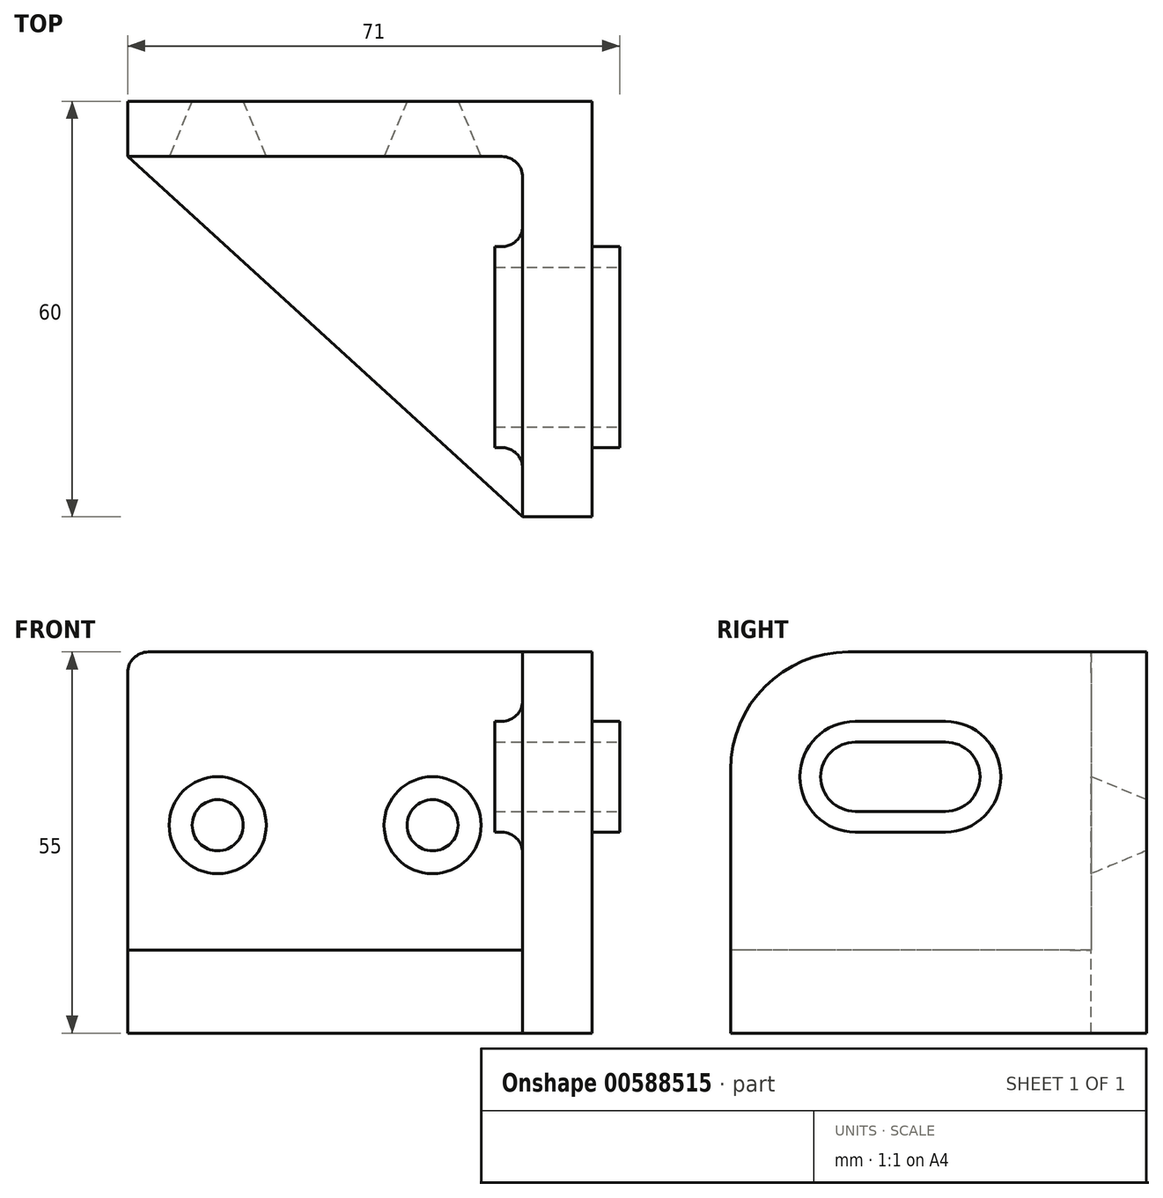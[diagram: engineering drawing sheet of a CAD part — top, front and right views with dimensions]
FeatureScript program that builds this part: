
annotation { "Feature Type Name" : "Feature", "Feature Type Description" : "" }
export const myFeature = defineFeature(function(context is Context, id is Id, definition is map)
    precondition{}
    {
        {
            var Q0;
            Q0=qCreatedBy(makeId("Top.planeOp"),FACE);
            var sketch = newSketch(context, id + "F0", { "sketchPlane" : qUnion([Q0])});
            skLineSegment(sketch, "E0.bottom", {"start": v(0, 0) * mm, "end": v(67, 0) * mm});
            skLineSegment(sketch, "E0.top", {"start": v(57, -60) * mm, "end": v(67, -60) * mm});
            skLineSegment(sketch, "E0.left", {"start": v(0, 0) * mm, "end": v(0, -8) * mm});
            skLineSegment(sketch, "E0.right", {"start": v(67, 0) * mm, "end": v(67, -60) * mm});
            skLineSegment(sketch, "E1", {"start": v(0, -8) * mm, "end": v(57, -60) * mm});
            skLineSegment(sketch, "E2", {"start": v(0, -8) * mm, "end": v(57, -8) * mm});
            skLineSegment(sketch, "E3", {"start": v(57, -8) * mm, "end": v(57, -60) * mm});
            skLineSegment(sketch, "E4.bottom", {"start": v(67, 0) * mm, "end": v(0, 0) * mm});
            skLineSegment(sketch, "E4.top", {"start": v(67, 5) * mm, "end": v(0, 5) * mm});
            skLineSegment(sketch, "E4.left", {"start": v(67, 0) * mm, "end": v(67, 5) * mm});
            skLineSegment(sketch, "E4.right", {"start": v(0, 0) * mm, "end": v(0, 5) * mm});
            skSolve(sketch);
        }
        {
            var Q0;
            {var subQ1=sQuery(id+"F0.wireOp",EDGE,"E1");Q0=makeQuery(id+"F0.imprint","IMPRINT",FACE,{"disambiguationData":[TD([[makeQuery(id+"F0.imprint","IMPRINT",EDGE,{"derivedFrom":subQ1}),1.0]])]});}
            var Q1;
            Q1=makeQuery(id+"F0.imprint","IMPRINT",FACE,{"disambiguationData":[TD([[makeQuery(id+"F0.imprint","IMPRINT",EDGE,{"derivedFrom":sQuery(id+"F0.wireOp",EDGE,"E0.left")}),1.0]])]});
            var Q2;
            Q2=makeQuery(id+"F0.imprint","IMPRINT",FACE,{"disambiguationData":[TD([[makeQuery(id+"F0.imprint","IMPRINT",EDGE,{"derivedFrom":sQuery(id+"F0.wireOp",EDGE,"E4.bottom")}),-1.0]])]});
            var Q3;
            {var subQ0=sQuery(id+"F0.wireOp",EDGE,"E0.top");Q3=makeQuery(id+"F0.imprint","IMPRINT",FACE,{"disambiguationData":[TD([[makeQuery(id+"F0.imprint","IMPRINT",EDGE,{"derivedFrom":subQ0}),1.0]])]});}
            var Q4;
            {var subQ0=sQuery(id+"F0.wireOp",EDGE,"VNKDlEv6-xTZ3-Mihn-J32e-wtWmNRO4bZqF.bottom");var subQ1=sQuery(id+"F0.wireOp",EDGE,"E0.right");var subQ2=makeQuery(id+"F0.imprint","INTERSECT",VERTEX,{"derivedFrom":[subQ1,subQ0]});Q4=makeQuery(id+"F0.imprint","IMPRINT",FACE,{"disambiguationData":[TD([[makeQuery(id+"F0.imprint","IMPRINT",EDGE,{"disambiguationData":[TD([[subQ2,-1.0]])],"derivedFrom":subQ1}),-1.0]])]});}
            var Q5;
            {var subQ5=sQuery(id+"F0.wireOp",EDGE,"VNKDlEv6-xTZ3-Mihn-J32e-wtWmNRO4bZqF.right");Q5=makeQuery(id+"F0.imprint","IMPRINT",FACE,{"disambiguationData":[TD([[makeQuery(id+"F0.imprint","IMPRINT",EDGE,{"derivedFrom":subQ5}),1.0]])]});}
            extrude(context, id + "F1", {"entities" : qUnion([Q0, Q1, Q2, Q3, Q4, Q5]), "oppositeDirection" : true, "depth" : 12 * mm, "offsetDistance" : 25 * mm});
        }
        {
            var Q0;
            Q0=makeQuery(id+"F0.imprint","IMPRINT",FACE,{"disambiguationData":[TD([[makeQuery(id+"F0.imprint","IMPRINT",EDGE,{"derivedFrom":sQuery(id+"F0.wireOp",EDGE,"E0.left")}),1.0]])]});
            var Q1;
            Q1=makeQuery(id+"F0.imprint","IMPRINT",FACE,{"disambiguationData":[TD([[makeQuery(id+"F0.imprint","IMPRINT",EDGE,{"derivedFrom":sQuery(id+"F0.wireOp",EDGE,"E4.bottom")}),-1.0]])]});
            var Q2;
            {var subQ0=sQuery(id+"F0.wireOp",EDGE,"VNKDlEv6-xTZ3-Mihn-J32e-wtWmNRO4bZqF.bottom");var subQ1=sQuery(id+"F0.wireOp",EDGE,"E0.right");var subQ2=makeQuery(id+"F0.imprint","INTERSECT",VERTEX,{"derivedFrom":[subQ1,subQ0]});Q2=makeQuery(id+"F0.imprint","IMPRINT",FACE,{"disambiguationData":[TD([[makeQuery(id+"F0.imprint","IMPRINT",EDGE,{"disambiguationData":[TD([[subQ2,-1.0]])],"derivedFrom":subQ1}),-1.0]])]});}
            var Q3;
            {var subQ0=sQuery(id+"F0.wireOp",EDGE,"E0.top");Q3=makeQuery(id+"F0.imprint","IMPRINT",FACE,{"disambiguationData":[TD([[makeQuery(id+"F0.imprint","IMPRINT",EDGE,{"derivedFrom":subQ0}),1.0]])]});}
            var Q4;
            {var subQ5=sQuery(id+"F0.wireOp",EDGE,"VNKDlEv6-xTZ3-Mihn-J32e-wtWmNRO4bZqF.right");Q4=makeQuery(id+"F0.imprint","IMPRINT",FACE,{"disambiguationData":[TD([[makeQuery(id+"F0.imprint","IMPRINT",EDGE,{"derivedFrom":subQ5}),1.0]])]});}
            var Q5;
            {var subQ5=sQuery(id+"F0.wireOp",EDGE,"VNKDlEv6-xTZ3-Mihn-J32e-wtWmNRO4bZqF.left");Q5=makeQuery(id+"F0.imprint","IMPRINT",FACE,{"disambiguationData":[TD([[makeQuery(id+"F0.imprint","IMPRINT",EDGE,{"derivedFrom":subQ5}),-1.0]])]});}
            extrude(context, id + "F2", {"entities" : qUnion([Q0, Q1, Q2, Q3, Q4, Q5]), "operationType" : NewBodyOperationType.ADD, "depth" : 43 * mm, "offsetDistance" : 25 * mm});
        }
        {
            var Q0;
            Q0=makeQuery(id+"F2.opExtrude","SWEPT_FACE",FACE,{"disambiguationData":[OSD([sQuery(id+"F0.wireOp",EDGE,"E3")])]});
            var Q1;
            {var subQ0=sQuery(id+"F0.wireOp",EDGE,"E4.left");var subQ1=sQuery(id+"F0.wireOp",EDGE,"E0.right");Q1=makeQuery(id+"F2.boolean.opBoolean","MERGE",FACE,{"derivedFrom":[makeQuery(id+"F1.opExtrude","SWEPT_FACE",FACE,{"disambiguationData":[OSD([subQ1,subQ0])]}),makeQuery(id+"F2.opExtrude","SWEPT_FACE",FACE,{"disambiguationData":[OSD([subQ1,subQ0])]})]});}
            cPlane(context, id + "F3", {"entities" : qUnion([Q0, Q1]), "cplaneType" : CPlaneType.MID_PLANE, "offset" : 25 * mm, "width" : 150 * mm, "height" : 150 * mm});
        }
        {
            var Q0;
            Q0=qCreatedBy(id+"F3.planeOp",FACE);
            var sketch = newSketch(context, id + "F4", { "sketchPlane" : qUnion([Q0])});
            skArc(sketch, "E5", {"start": v(42, 20) * mm, "mid": v(47, 25) * mm, "end": v(42, 30) * mm});
            skArc(sketch, "E6", {"start": v(29, 30) * mm, "mid": v(24, 25) * mm, "end": v(29, 20) * mm});
            skArc(sketch, "E7", {"start": v(29, 33) * mm, "mid": v(21, 25) * mm, "end": v(29, 17) * mm});
            skLineSegment(sketch, "E8", {"start": v(29, 33) * mm, "end": v(42, 33) * mm});
            skLineSegment(sketch, "E9", {"start": v(29, 17) * mm, "end": v(42, 17) * mm});
            skLineSegment(sketch, "E10", {"start": v(29, 30) * mm, "end": v(42, 30) * mm});
            skLineSegment(sketch, "E11", {"start": v(29, 20) * mm, "end": v(42, 20) * mm});
            skArc(sketch, "E12.trimOffspring", {"start": v(42, 17) * mm, "mid": v(50, 25) * mm, "end": v(42, 33) * mm});
            skPoint(sketch, "E13", {"position": v(43, 43) * mm});
            skPoint(sketch, "E14", {"position": v(60, 26) * mm});
            skSolve(sketch);
        }
        {
            var Q0;
            Q0 = qSketchRegion(id + "F4", true);
            extrude(context, id + "F5", {"entities" : qUnion([Q0]), "operationType" : NewBodyOperationType.ADD, "depth" : 18 * mm, "offsetDistance" : 25 * mm, "symmetric" : true});
        }
        {
            var Q0;
            Q0=qCreatedBy(id+"F3.planeOp",FACE);
            var sketch = newSketch(context, id + "F6", { "sketchPlane" : qUnion([Q0])});
            skArc(sketch, "E15", {"start": v(60, 26) * mm, "mid": v(55.02, 38.02) * mm, "end": v(43, 43) * mm});
            skPoint(sketch, "E16", {"position": v(43, 43) * mm});
            skPoint(sketch, "E17", {"position": v(60, 26) * mm});
            skLineSegment(sketch, "E18", {"start": v(43, 43) * mm, "end": v(60, 43) * mm});
            skLineSegment(sketch, "E19", {"start": v(60, 43) * mm, "end": v(60, 26) * mm});
            skArc(sketch, "E20", {"start": v(29, 30) * mm, "mid": v(24, 25) * mm, "end": v(29, 20) * mm});
            skArc(sketch, "E21", {"start": v(42, 20) * mm, "mid": v(47, 25) * mm, "end": v(42, 30) * mm});
            skLineSegment(sketch, "E22", {"start": v(29, 30) * mm, "end": v(42, 30) * mm});
            skLineSegment(sketch, "E23", {"start": v(29, 20) * mm, "end": v(42, 20) * mm});
            skLineSegment(sketch, "E24.bottom", {"start": v(-5, -12) * mm, "end": v(0, -12) * mm});
            skLineSegment(sketch, "E24.top", {"start": v(-5, 30) * mm, "end": v(0, 30) * mm});
            skLineSegment(sketch, "E24.left", {"start": v(-5, -12) * mm, "end": v(-5, 30) * mm});
            skLineSegment(sketch, "E24.right", {"start": v(0, -12) * mm, "end": v(0, 30) * mm});
            skSolve(sketch);
        }
        {
            var Q0;
            Q0 = qSketchRegion(id + "F6", true);
            extrude(context, id + "F7", {"entities" : qUnion([Q0]), "operationType" : NewBodyOperationType.REMOVE, "oppositeDirection" : true, "depth" : 200 * mm, "offsetDistance" : 25 * mm, "symmetric" : true});
        }
        {
            var Q0;
            Q0=makeQuery(id+"F2.opExtrude","SWEPT_FACE",FACE,{"disambiguationData":[OSD([sQuery(id+"F0.wireOp",EDGE,"E2")])]});
            var sketch = newSketch(context, id + "F8", { "sketchPlane" : qUnion([Q0])});
            skPoint(sketch, "E25", {"position": v(13, 18) * mm});
            skPoint(sketch, "E26", {"position": v(44, 18) * mm});
            skSolve(sketch);
        }
        {
            var Q0;
            Q0=sQuery(id+"F8.wireOp",VERTEX,"E25");
            var Q1;
            Q1=sQuery(id+"F8.wireOp",VERTEX,"E26");
            var Q2;
            Q2=makeQuery(id+"F1.opExtrude","SWEPT_BODY",BODY,{"disambiguationData":[OSD([sQuery(id+"F0.wireOp",EDGE,"E0.top"),sQuery(id+"F0.wireOp",EDGE,"E0.left"),sQuery(id+"F0.wireOp",EDGE,"E0.right"),sQuery(id+"F0.wireOp",EDGE,"E1"),sQuery(id+"F0.wireOp",EDGE,"E4.top"),sQuery(id+"F0.wireOp",EDGE,"E4.left"),sQuery(id+"F0.wireOp",EDGE,"E4.right")])]});
            hole(context, id + "F9", {"style" : HoleStyle.C_SINK, "endStyle" : HoleEndStyle.THROUGH, "holeDiameter" : 5 * mm, "cSinkDiameter" : 14 * mm, "cSinkAngle" : 45 * degree, "majorDiameter" : 5 * mm, "isTappedThrough" : true, "tappedDepth" : 12 * mm, "tapClearance" : 3, "locations" : qUnion([Q0, Q1]), "scope" : qUnion([Q2])});
        }
        {
            var Q0;
            Q0=makeQuery(id+"F5.boolean.opBoolean","INTERSECT",EDGE,{"derivedFrom":[makeQuery(id+"F2.opExtrude","SWEPT_FACE",FACE,{"disambiguationData":[OSD([sQuery(id+"F0.wireOp",EDGE,"E3")])]}),makeQuery(id+"F5.opExtrude","SWEPT_FACE",FACE,{"disambiguationData":[OSD([sQuery(id+"F4.wireOp",EDGE,"E7")])]})]});
            var Q1;
            Q1=makeQuery(id+"F5.boolean.opBoolean","INTERSECT",EDGE,{"derivedFrom":[makeQuery(id+"F2.opExtrude","SWEPT_FACE",FACE,{"disambiguationData":[OSD([sQuery(id+"F0.wireOp",EDGE,"E3")])]}),makeQuery(id+"F5.opExtrude","SWEPT_FACE",FACE,{"disambiguationData":[OSD([sQuery(id+"F4.wireOp",EDGE,"E8")])]})]});
            var Q2;
            Q2=makeQuery(id+"F2.opExtrude","CAP_EDGE",EDGE,{"disambiguationData":[OSD([sQuery(id+"F0.wireOp",EDGE,"E3")])],"isStart":true});
            var Q3;
            Q3=makeQuery(id+"F2.opExtrude","CAP_EDGE",EDGE,{"disambiguationData":[OSD([sQuery(id+"F0.wireOp",EDGE,"E2")])],"isStart":true});
            var Q4;
            Q4=makeQuery(id+"F2.opExtrude","SWEPT_EDGE",EDGE,{"disambiguationData":[OSD([sQuery(id+"F0.wireOp",EDGE,"E2"),sQuery(id+"F0.wireOp",EDGE,"E3")])]});
            var Q5;
            Q5=makeQuery(id+"F2.opExtrude","CAP_EDGE",EDGE,{"disambiguationData":[OSD([sQuery(id+"F0.wireOp",EDGE,"E0.left"),sQuery(id+"F0.wireOp",EDGE,"E4.right")])],"isStart":false});
            fillet(context, id + "F10", {"entities" : qUnion([Q0, Q1, Q2, Q3, Q4, Q5]), "radius" : 3 * mm, "tangentPropagation" : true, "allowEdgeOverflow" : false});
        }
    });
